# Revit family: ST-140 CONCENTRIC REDUCER GROOVED
name_source: partatom
category: Pipe Fittings
units: mm (PartAtom-declared; Revit-internal decimal feet)

## family parameters
Always vertical = No
Cut with Voids When Loaded = No
Part Type = Transition
Round Connector Dimension = Use Diameter
Shared = No
Work Plane-Based = No

## types (48) — shared parameters
zero-valued in all types: Default Elevation

## per-type parameters (varying)
| type | K Coefficient Table | Loss Method |
| 50X32 |  | Not Defined |
| 50X40 |  | Not Defined |
| 32X25 |  | Not Defined |
| 40X25 |  | Not Defined |
| 50X25 | Reducer/Coupling/Union/Increaser | K Coefficient |
| 65X32 |  | Not Defined |
| 65X40 |  | Not Defined |
| 65X50 |  | Not Defined |
| 76.1X32 |  | Not Defined |
| 76.1X40 |  | Not Defined |
| 76.1X50 |  | Not Defined |
| 80X32 |  | Not Defined |
| 80X40 |  | Not Defined |
| 80X50 |  | Not Defined |
| 80X65 |  | Not Defined |
| 100X32 |  | Not Defined |
| 100X40 |  | Not Defined |
| 100X50 |  | Not Defined |
| 100X76.1 |  | Not Defined |
| 100X65 |  | Not Defined |
| 100X80 |  | Not Defined |
| 125X50 |  | Not Defined |
| 125X76.1 |  | Not Defined |
| 125X65 |  | Not Defined |
| 125X80 |  | Not Defined |
| 125X100 |  | Not Defined |
| 165.1X50 |  | Not Defined |
| 165.1X76.1 |  | Not Defined |
| 165.1X65 |  | Not Defined |
| 165.1X100 |  | Not Defined |
| 150X50 |  | Not Defined |
| 150X76.1 |  | Not Defined |
| 150X65 |  | Not Defined |
| 150X80 |  | Not Defined |
| 150X100 |  | Not Defined |
| 150X125 |  | Not Defined |
| 80X76.1 |  | Not Defined |
| 200X80 |  | Not Defined |
| 200X100 |  | Not Defined |
| 200X125 |  | Not Defined |
| 200X150 |  | Not Defined |
| 200X165.1 |  | Not Defined |
| 250X80 |  | Not Defined |
| 250X100 |  | Not Defined |
| 250X125 |  | Not Defined |
| 250X150 |  | Not Defined |
| 250X165.1 |  | Not Defined |
| 250X200 |  | Not Defined |

## geometry (parser evidence)
native form markers: Sweep x3
no freeform markers — native parametric forms only
